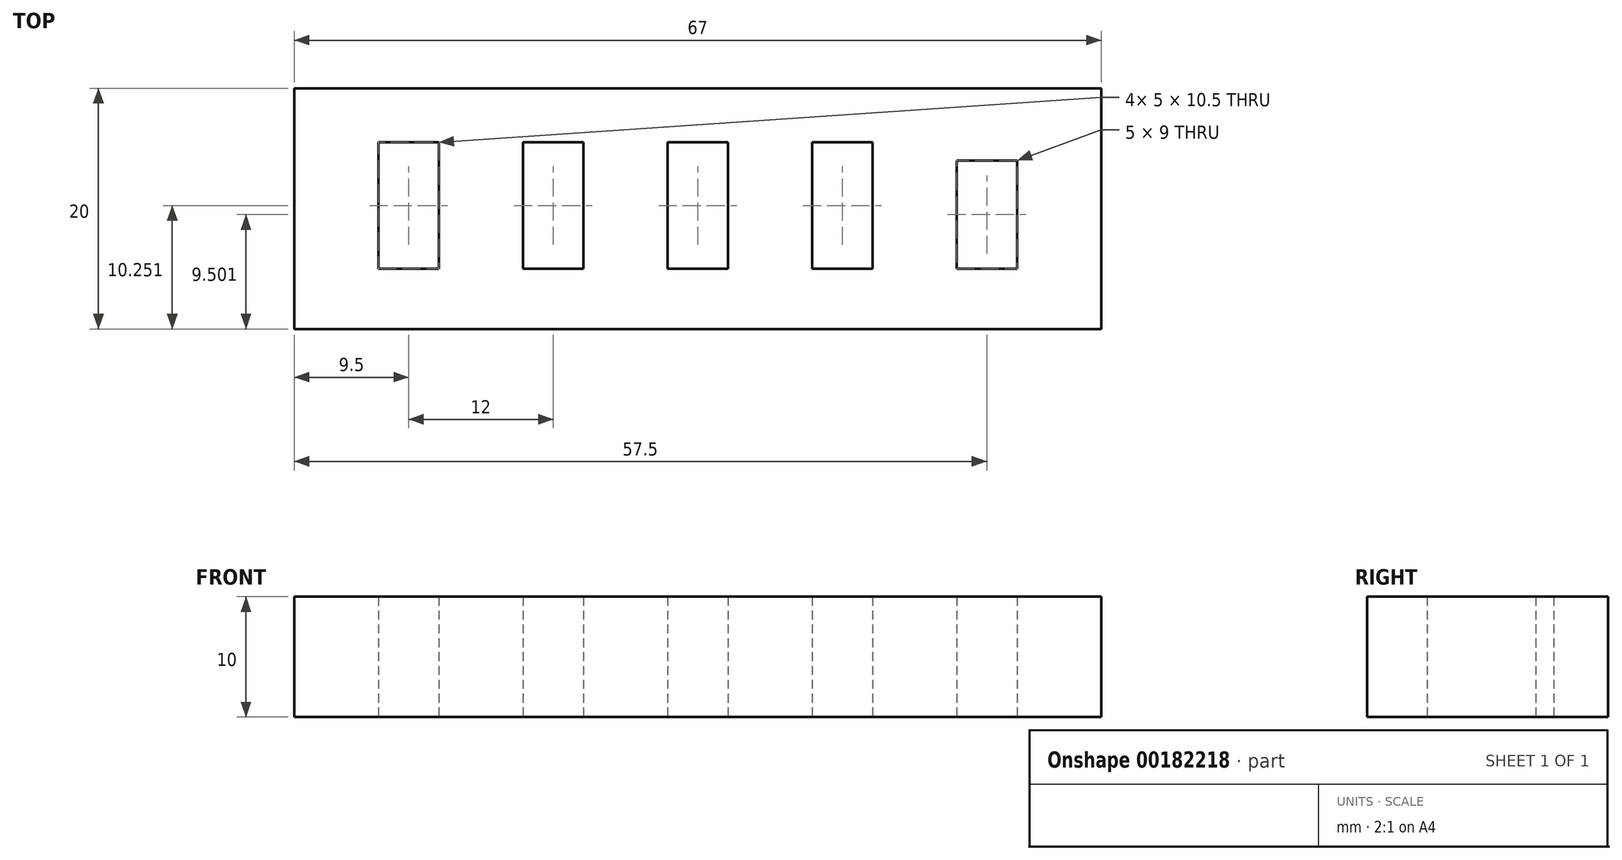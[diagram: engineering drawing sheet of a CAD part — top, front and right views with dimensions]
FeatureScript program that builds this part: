
annotation { "Feature Type Name" : "Feature", "Feature Type Description" : "" }
export const myFeature = defineFeature(function(context is Context, id is Id, definition is map)
    precondition{}
    {
        {
            var Q0;
            Q0=qCreatedBy(makeId("Top.planeOp"),FACE);
            var sketch = newSketch(context, id + "F0", { "sketchPlane" : qUnion([Q0])});
            skLineSegment(sketch, "E0.bottom", {"start": v(-31, 11.03) * mm, "end": v(36, 11.03) * mm});
            skLineSegment(sketch, "E0.top", {"start": v(-31, -8.97) * mm, "end": v(36, -8.97) * mm});
            skLineSegment(sketch, "E0.left", {"start": v(-31, 11.03) * mm, "end": v(-31, -8.97) * mm});
            skLineSegment(sketch, "E0.right", {"start": v(36, 11.03) * mm, "end": v(36, -8.97) * mm});
            skLineSegment(sketch, "E1.bottom", {"start": v(-24, 6.53) * mm, "end": v(-19, 6.53) * mm});
            skLineSegment(sketch, "E1.top", {"start": v(-24, -3.97) * mm, "end": v(-19, -3.97) * mm});
            skLineSegment(sketch, "E1.left", {"start": v(-24, 6.53) * mm, "end": v(-24, -3.97) * mm});
            skLineSegment(sketch, "E1.right", {"start": v(-19, 6.53) * mm, "end": v(-19, -3.97) * mm});
            skLineSegment(sketch, "E2.bottom", {"start": v(-12, 6.53) * mm, "end": v(-7, 6.53) * mm});
            skLineSegment(sketch, "E2.top", {"start": v(-12, -3.97) * mm, "end": v(-7, -3.97) * mm});
            skLineSegment(sketch, "E2.left", {"start": v(-12, 6.53) * mm, "end": v(-12, -3.97) * mm});
            skLineSegment(sketch, "E2.right", {"start": v(-7, 6.53) * mm, "end": v(-7, -3.97) * mm});
            skLineSegment(sketch, "E3.bottom", {"start": v(0, 6.53) * mm, "end": v(5, 6.53) * mm});
            skLineSegment(sketch, "E3.top", {"start": v(0, -3.97) * mm, "end": v(5, -3.97) * mm});
            skLineSegment(sketch, "E3.left", {"start": v(0, 6.53) * mm, "end": v(0, -3.97) * mm});
            skLineSegment(sketch, "E3.right", {"start": v(5, 6.53) * mm, "end": v(5, -3.97) * mm});
            skLineSegment(sketch, "E4.bottom", {"start": v(12, 6.53) * mm, "end": v(17, 6.53) * mm});
            skLineSegment(sketch, "E4.top", {"start": v(12, -3.97) * mm, "end": v(17, -3.97) * mm});
            skLineSegment(sketch, "E4.left", {"start": v(12, 6.53) * mm, "end": v(12, -3.97) * mm});
            skLineSegment(sketch, "E4.right", {"start": v(17, 6.53) * mm, "end": v(17, -3.97) * mm});
            skLineSegment(sketch, "E5.bottom", {"start": v(24, 5.03) * mm, "end": v(29, 5.03) * mm});
            skLineSegment(sketch, "E5.top", {"start": v(24, -3.97) * mm, "end": v(29, -3.97) * mm});
            skLineSegment(sketch, "E5.left", {"start": v(24, 5.03) * mm, "end": v(24, -3.97) * mm});
            skLineSegment(sketch, "E5.right", {"start": v(29, 5.03) * mm, "end": v(29, -3.97) * mm});
            skSolve(sketch);
        }
        {
            var Q0;
            Q0=makeQuery(id+"F0.imprint","IMPRINT",FACE,{"disambiguationData":[TD([[makeQuery(id+"F0.imprint","IMPRINT",EDGE,{"derivedFrom":sQuery(id+"F0.wireOp",EDGE,"E0.bottom")}),-1.0]])]});
            extrude(context, id + "F1", {"entities" : qUnion([Q0]), "depth" : 10 * mm});
        }
    });
